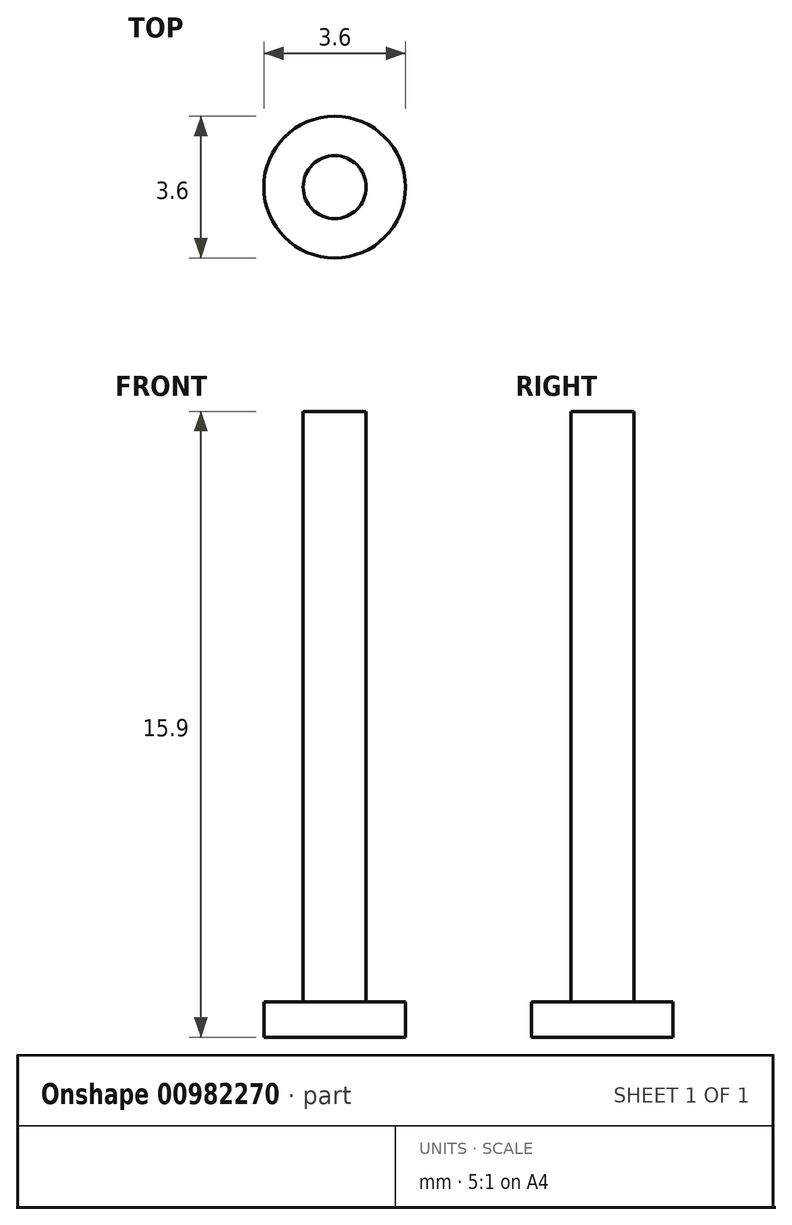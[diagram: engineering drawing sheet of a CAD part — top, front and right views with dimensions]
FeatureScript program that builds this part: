
annotation { "Feature Type Name" : "Feature", "Feature Type Description" : "" }
export const myFeature = defineFeature(function(context is Context, id is Id, definition is map)
    precondition{}
    {
        {
            var Q0;
            Q0=qCreatedBy(makeId("Top.planeOp"),FACE);
            var sketch = newSketch(context, id + "F0", { "sketchPlane" : qUnion([Q0])});
            skCircle(sketch, "E0", {"center": v(0, 0) * mm, "radius": 1.8 * mm});
            skSolve(sketch);
        }
        {
            var Q0;
            Q0 = qSketchRegion(id + "F0", true);
            extrude(context, id + "F1", {"entities" : qUnion([Q0]), "depth" : .9 * mm, "offsetDistance" : 25 * mm});
        }
        {
            var Q0;
            Q0=makeQuery(id+"F1.opExtrude","CAP_FACE",FACE,{"disambiguationData":[OSD([sQuery(id+"F0.wireOp",EDGE,"E0")])],"isStart":false});
            var sketch = newSketch(context, id + "F2", { "sketchPlane" : qUnion([Q0])});
            skCircle(sketch, "E1", {"center": v(0, 0) * mm, "radius": 0.8 * mm});
            skSolve(sketch);
        }
        {
            var Q0;
            Q0 = qSketchRegion(id + "F2", true);
            extrude(context, id + "F3", {"entities" : qUnion([Q0]), "operationType" : NewBodyOperationType.ADD, "depth" : 15 * mm, "offsetDistance" : 25 * mm});
        }
    });
